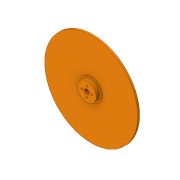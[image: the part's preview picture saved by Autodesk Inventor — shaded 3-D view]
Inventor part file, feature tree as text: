
AUTODESK INVENTOR PART (.ipt)
format: ipt  version: 2016 (Build 200138000, 138)  size: 115,200 bytes
history: native  units: in
note: dims shown in document units (in); Inventor stores cm internally (conversion verified against a paired STEP export)
features: sketch x5, extrude x4, reference x2, other x1, hole x1
ambient origin geometry x8: Origin, YZ Plane, XZ Plane, XY Plane, X Axis, Y Axis, Z Axis, Center Point
bodies: Solid1 (feature_tree)
feature tree (13):
  other  "skeleton.ipt"
  extrude  "Extrusion1"  Depth=0.3937in
  extrude  "Extrusion2"  Depth=0.1181in
  extrude  "Extrusion4"  Depth=0.0394in
  hole  "Hole2"  [1 undecoded]
  extrude  "Extrusion5"  Depth=0.3937in TaperAngle=0.0deg
  sketch  "Sketch2"  dims[d0=0.3937in d1=5.9055in]
  sketch  "Sketch4"  dims[d2=0.1181in d3=0.0in d11=1.4173in]
  sketch  "Sketch6"  dims[d12=0.0394in d13=0.0in d18=1.1811in]
  sketch  "Sketch7"  dims[d19=0.2362in d20=0.0in]
  reference  "Reference2"
  sketch  "Sketch8"  dims[d21=0.1024in d22=0.2362in d23=0.1575in d24=0.0787in d25=90.0deg d26=0.315in d27=0.8108in d28=0.315in d29=0.3937in d30=0.0in]
  reference  "Reference3"
note: 1 required parameter value undecoded (feature->parameter linkage not recoverable at this tier; creation-order binding heuristic only, values carry confidence <= 0.55)
